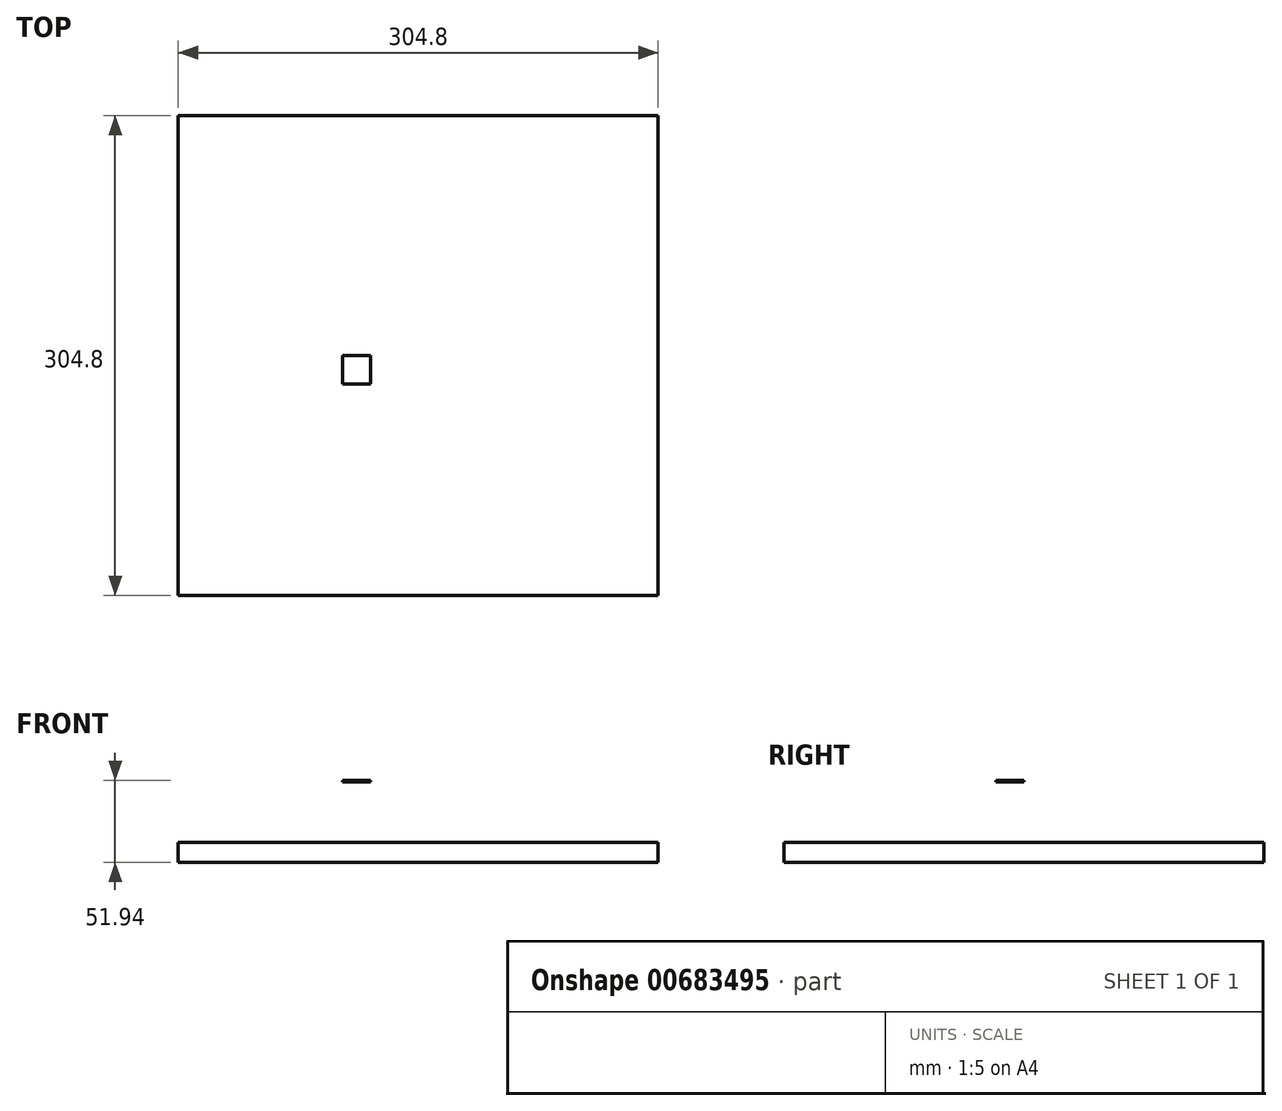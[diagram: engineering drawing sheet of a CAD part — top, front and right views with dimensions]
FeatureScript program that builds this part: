
annotation { "Feature Type Name" : "Feature", "Feature Type Description" : "" }
export const myFeature = defineFeature(function(context is Context, id is Id, definition is map)
    precondition{}
    {
        {
            var Q0;
            Q0=qCreatedBy(makeId("Top.planeOp"),FACE);
            var sketch = newSketch(context, id + "F0", { "sketchPlane" : qUnion([Q0])});
            skLineSegment(sketch, "E0.bottom", {"start": v(152.4, -152.4) * mm, "end": v(-152.4, -152.4) * mm});
            skLineSegment(sketch, "E0.top", {"start": v(152.4, 152.4) * mm, "end": v(-152.4, 152.4) * mm});
            skLineSegment(sketch, "E0.left", {"start": v(152.4, -152.4) * mm, "end": v(152.4, 152.4) * mm});
            skLineSegment(sketch, "E0.right", {"start": v(-152.4, -152.4) * mm, "end": v(-152.4, 152.4) * mm});
            skPoint(sketch, "E0.middle", {"position": v(0, 0) * mm});
            skSolve(sketch);
        }
        {
            var Q0;
            Q0 = qSketchRegion(id + "F0", true);
            extrude(context, id + "F1", {"entities" : qUnion([Q0]), "depth" : 12.7 * mm, "offsetDistance" : 25 * mm});
        }
        {
            var Q0;
            Q0=qCreatedBy(makeId("Front.planeOp"),FACE);
            var sketch = newSketch(context, id + "F2", { "sketchPlane" : qUnion([Q0])});
            skLineSegment(sketch, "E1", {"start": v(-48.17, 51.94) * mm, "end": v(-30.17, 51.94) * mm});
            skLineSegment(sketch, "E2", {"start": v(-30.17, 51.94) * mm, "end": v(-30.17, 50.94) * mm});
            skLineSegment(sketch, "E3", {"start": v(-48.17, 51.94) * mm, "end": v(-48.17, 50.94) * mm});
            skLineSegment(sketch, "E4", {"start": v(-48.17, 50.94) * mm, "end": v(-30.17, 50.94) * mm});
            skSolve(sketch);
        }
        {
            var Q0;
            Q0 = qSketchRegion(id + "F2", true);
            extrude(context, id + "F3", {"entities" : qUnion([Q0]), "depth" : 18 * mm, "offsetDistance" : 25 * mm});
        }
    });
